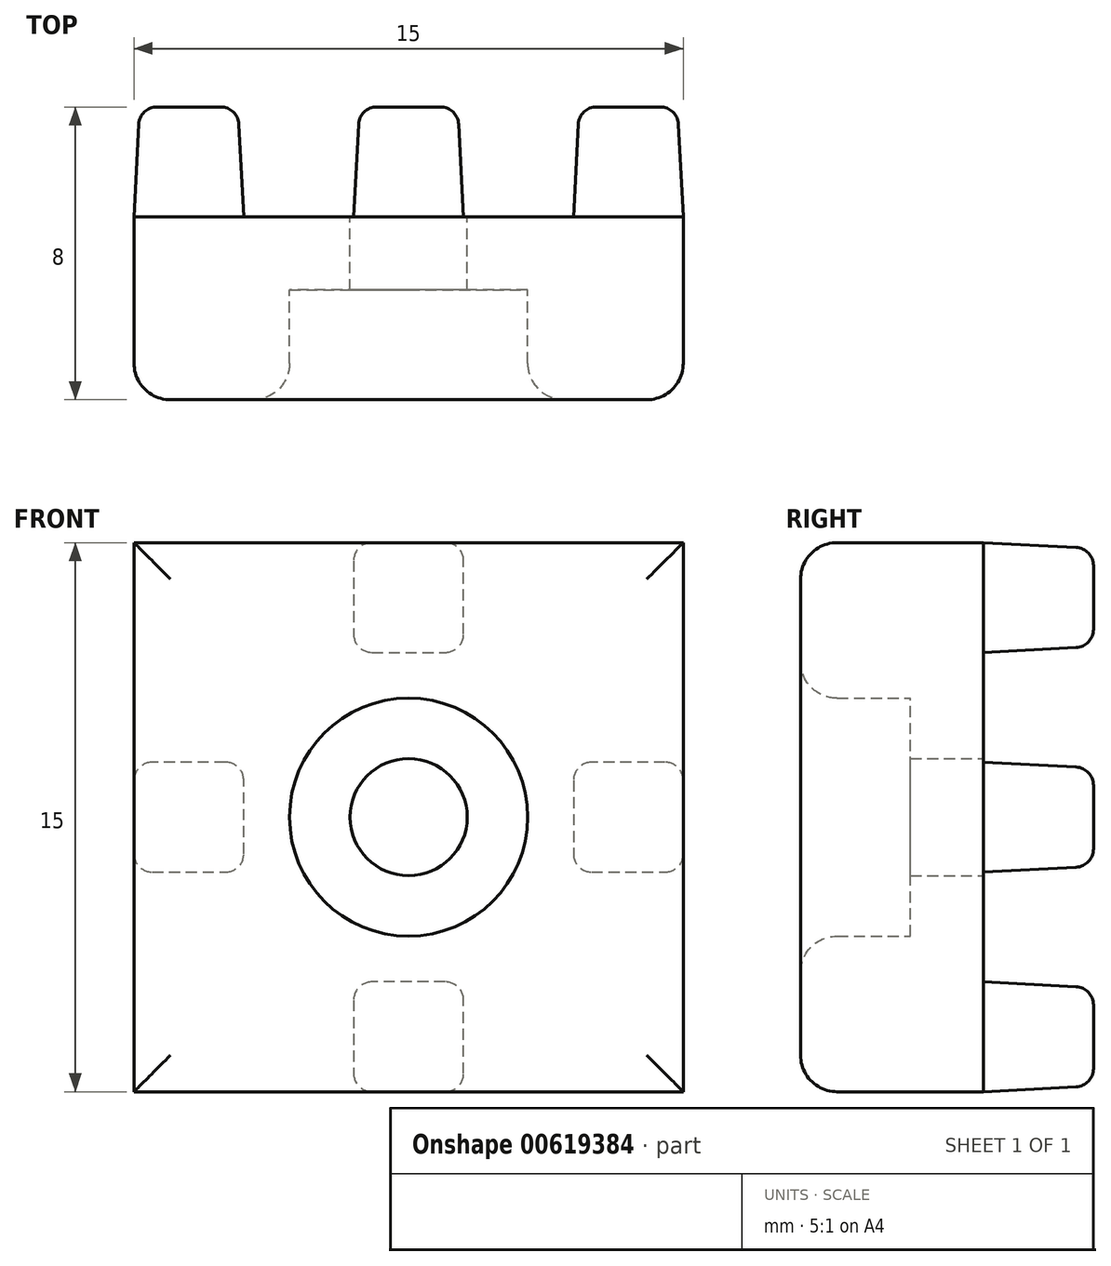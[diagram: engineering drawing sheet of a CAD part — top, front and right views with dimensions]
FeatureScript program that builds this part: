
annotation { "Feature Type Name" : "Feature", "Feature Type Description" : "" }
export const myFeature = defineFeature(function(context is Context, id is Id, definition is map)
    precondition{}
    {
        {
            var Q0;
            Q0=qCreatedBy(makeId("Front.planeOp"),FACE);
            var sketch = newSketch(context, id + "F0", { "sketchPlane" : qUnion([Q0])});
            skLineSegment(sketch, "E0.bottom", {"start": v(0, 0) * mm, "end": v(15, 0) * mm});
            skLineSegment(sketch, "E0.top", {"start": v(0, 15) * mm, "end": v(15, 15) * mm});
            skLineSegment(sketch, "E0.left", {"start": v(0, 0) * mm, "end": v(0, 15) * mm});
            skLineSegment(sketch, "E0.right", {"start": v(15, 0) * mm, "end": v(15, 15) * mm});
            skCircle(sketch, "E1", {"center": v(7.5, 7.5) * mm, "radius": 1.6 * mm});
            skPoint(sketch, "E1.centerSnap0", {"position": v(0, 7.5) * mm});
            skPoint(sketch, "E1.centerSnap1", {"position": v(7.5, 15) * mm});
            skCircle(sketch, "E2", {"center": v(7.5, 7.5) * mm, "radius": 3.25 * mm});
            skLineSegment(sketch, "E3", {"start": v(6, 15) * mm, "end": v(6, 12) * mm});
            skLineSegment(sketch, "E4", {"start": v(6, 12) * mm, "end": v(7.5, 12) * mm});
            skLineSegment(sketch, "E5", {"start": v(7.5, 15) * mm, "end": v(7.5, 12) * mm, "construction": true});
            skLineSegment(sketch, "E6.MirrorCS", {"start": v(9, 12) * mm, "end": v(7.5, 12) * mm});
            skLineSegment(sketch, "E7.MirrorCS", {"start": v(9, 15) * mm, "end": v(9, 12) * mm});
            skLineSegment(sketch, "E8.1.0", {"start": v(3, 6) * mm, "end": v(3, 7.5) * mm});
            skLineSegment(sketch, "E8.1.1", {"start": v(0, 6) * mm, "end": v(3, 6) * mm});
            skLineSegment(sketch, "E8.1.2", {"start": v(3, 9) * mm, "end": v(3, 7.5) * mm});
            skLineSegment(sketch, "E8.1.3", {"start": v(0, 9) * mm, "end": v(3, 9) * mm});
            skLineSegment(sketch, "E8.2.0", {"start": v(9, 3) * mm, "end": v(7.5, 3) * mm});
            skLineSegment(sketch, "E8.2.1", {"start": v(9, 0) * mm, "end": v(9, 3) * mm});
            skLineSegment(sketch, "E8.2.2", {"start": v(6, 3) * mm, "end": v(7.5, 3) * mm});
            skLineSegment(sketch, "E8.2.3", {"start": v(6, 0) * mm, "end": v(6, 3) * mm});
            skLineSegment(sketch, "E8.3.0", {"start": v(12, 9) * mm, "end": v(12, 7.5) * mm});
            skLineSegment(sketch, "E8.3.1", {"start": v(15, 9) * mm, "end": v(12, 9) * mm});
            skLineSegment(sketch, "E8.3.2", {"start": v(12, 6) * mm, "end": v(12, 7.5) * mm});
            skLineSegment(sketch, "E8.3.3", {"start": v(15, 6) * mm, "end": v(12, 6) * mm});
            skSolve(sketch);
        }
        {
            var Q0;
            Q0=makeQuery(id+"F0.imprint","IMPRINT",FACE,{"disambiguationData":[TD([[makeQuery(id+"F0.imprint","IMPRINT",EDGE,{"derivedFrom":sQuery(id+"F0.wireOp",EDGE,"E0.bottom")}),1.0]])]});
            var Q1;
            Q1=makeQuery(id+"F0.imprint","IMPRINT",FACE,{"disambiguationData":[TD([[makeQuery(id+"F0.imprint","IMPRINT",EDGE,{"derivedFrom":sQuery(id+"F0.wireOp",EDGE,"E8.2.0")}),1.0]])]});
            var Q2;
            Q2=makeQuery(id+"F0.imprint","IMPRINT",FACE,{"disambiguationData":[TD([[makeQuery(id+"F0.imprint","IMPRINT",EDGE,{"derivedFrom":sQuery(id+"F0.wireOp",EDGE,"E8.1.0")}),1.0]])]});
            var Q3;
            {var subQ0=sQuery(id+"F0.wireOp",EDGE,"E3");Q3=makeQuery(id+"F0.imprint","IMPRINT",FACE,{"disambiguationData":[TD([[makeQuery(id+"F0.imprint","IMPRINT",EDGE,{"derivedFrom":subQ0}),1.0]])]});}
            var Q4;
            Q4=makeQuery(id+"F0.imprint","IMPRINT",FACE,{"disambiguationData":[TD([[makeQuery(id+"F0.imprint","IMPRINT",EDGE,{"derivedFrom":sQuery(id+"F0.wireOp",EDGE,"E8.3.0")}),1.0]])]});
            extrude(context, id + "F1", {"entities" : qUnion([Q0, Q1, Q2, Q3, Q4]), "depth" : 5 * mm, "offsetDistance" : 25 * mm});
        }
        {
            var Q0;
            Q0=makeQuery(id+"F0.imprint","IMPRINT",FACE,{"disambiguationData":[TD([[makeQuery(id+"F0.imprint","IMPRINT",EDGE,{"derivedFrom":sQuery(id+"F0.wireOp",EDGE,"E1")}),-1.0]])]});
            extrude(context, id + "F2", {"entities" : qUnion([Q0]), "operationType" : NewBodyOperationType.ADD, "depth" : 2 * mm, "offsetDistance" : 25 * mm});
        }
        {
            var Q0;
            Q0=makeQuery(id+"F0.imprint","IMPRINT",FACE,{"disambiguationData":[TD([[makeQuery(id+"F0.imprint","IMPRINT",EDGE,{"derivedFrom":sQuery(id+"F0.wireOp",EDGE,"E8.2.0")}),1.0]])]});
            var Q1;
            Q1=makeQuery(id+"F0.imprint","IMPRINT",FACE,{"disambiguationData":[TD([[makeQuery(id+"F0.imprint","IMPRINT",EDGE,{"derivedFrom":sQuery(id+"F0.wireOp",EDGE,"E8.1.0")}),1.0]])]});
            var Q2;
            {var subQ0=sQuery(id+"F0.wireOp",EDGE,"E3");Q2=makeQuery(id+"F0.imprint","IMPRINT",FACE,{"disambiguationData":[TD([[makeQuery(id+"F0.imprint","IMPRINT",EDGE,{"derivedFrom":subQ0}),1.0]])]});}
            var Q3;
            Q3=makeQuery(id+"F0.imprint","IMPRINT",FACE,{"disambiguationData":[TD([[makeQuery(id+"F0.imprint","IMPRINT",EDGE,{"derivedFrom":sQuery(id+"F0.wireOp",EDGE,"E8.3.0")}),1.0]])]});
            extrude(context, id + "F3", {"entities" : qUnion([Q0, Q1, Q2, Q3]), "operationType" : NewBodyOperationType.ADD, "oppositeDirection" : true, "depth" : 3 * mm, "offsetDistance" : 25 * mm, "hasDraft" : true, "draftAngle" : 3 * degree, "draftPullDirection" : true});
        }
        {
            var Q0;
            Q0=makeQuery(id+"F1.opExtrude","CAP_EDGE",EDGE,{"disambiguationData":[OSD([sQuery(id+"F0.wireOp",EDGE,"E0.top")])],"isStart":false});
            var Q1;
            Q1=makeQuery(id+"F1.opExtrude","CAP_EDGE",EDGE,{"disambiguationData":[OSD([sQuery(id+"F0.wireOp",EDGE,"E0.right")])],"isStart":false});
            var Q2;
            Q2=makeQuery(id+"F1.opExtrude","CAP_EDGE",EDGE,{"disambiguationData":[OSD([sQuery(id+"F0.wireOp",EDGE,"E0.bottom")])],"isStart":false});
            var Q3;
            Q3=makeQuery(id+"F1.opExtrude","CAP_EDGE",EDGE,{"disambiguationData":[OSD([sQuery(id+"F0.wireOp",EDGE,"E0.left")])],"isStart":false});
            var Q4;
            Q4=makeQuery(id+"F1.opExtrude","CAP_EDGE",EDGE,{"disambiguationData":[OSD([sQuery(id+"F0.wireOp",EDGE,"E2")])],"isStart":false});
            fillet(context, id + "F4", {"entities" : qUnion([Q0, Q1, Q2, Q3, Q4]), "radius" : 1 * mm, "tangentPropagation" : true, "allowEdgeOverflow" : false});
        }
        {
            var Q0;
            Q0=makeQuery(id+"F3.opExtrude","CAP_EDGE",EDGE,{"disambiguationData":[OSD([sQuery(id+"F0.wireOp",EDGE,"E8.2.0"),sQuery(id+"F0.wireOp",EDGE,"E8.2.2")])],"isStart":false});
            var Q1;
            Q1=makeQuery(id+"F3.opExtrude","CAP_EDGE",EDGE,{"disambiguationData":[OSD([sQuery(id+"F0.wireOp",EDGE,"E8.2.3")])],"isStart":false});
            var Q2;
            Q2=makeQuery(id+"F3.opExtrude","CAP_EDGE",EDGE,{"disambiguationData":[OSD([sQuery(id+"F0.wireOp",EDGE,"E0.bottom")])],"isStart":false});
            var Q3;
            Q3=makeQuery(id+"F3.opExtrude","CAP_EDGE",EDGE,{"disambiguationData":[OSD([sQuery(id+"F0.wireOp",EDGE,"E8.2.1")])],"isStart":false});
            var Q4;
            Q4=makeQuery(id+"F3.opExtrude","SWEPT_EDGE",EDGE,{"disambiguationData":[OSD([sQuery(id+"F0.wireOp",EDGE,"E8.2.2"),sQuery(id+"F0.wireOp",EDGE,"E8.2.3")])]});
            var Q5;
            Q5=makeQuery(id+"F3.opExtrude","SWEPT_EDGE",EDGE,{"disambiguationData":[OSD([sQuery(id+"F0.wireOp",EDGE,"E8.2.0"),sQuery(id+"F0.wireOp",EDGE,"E8.2.1")])]});
            var Q6;
            Q6=makeQuery(id+"F3.opExtrude","SWEPT_EDGE",EDGE,{"disambiguationData":[OSD([sQuery(id+"F0.wireOp",EDGE,"E0.bottom"),sQuery(id+"F0.wireOp",EDGE,"E8.2.1")])]});
            var Q7;
            Q7=makeQuery(id+"F3.opExtrude","SWEPT_EDGE",EDGE,{"disambiguationData":[OSD([sQuery(id+"F0.wireOp",EDGE,"E0.bottom"),sQuery(id+"F0.wireOp",EDGE,"E8.2.3")])]});
            var Q8;
            Q8=makeQuery(id+"F3.opExtrude","SWEPT_EDGE",EDGE,{"disambiguationData":[OSD([sQuery(id+"F0.wireOp",EDGE,"E0.left"),sQuery(id+"F0.wireOp",EDGE,"E8.1.1")])]});
            var Q9;
            Q9=makeQuery(id+"F3.opExtrude","SWEPT_EDGE",EDGE,{"disambiguationData":[OSD([sQuery(id+"F0.wireOp",EDGE,"E0.left"),sQuery(id+"F0.wireOp",EDGE,"E8.1.3")])]});
            var Q10;
            Q10=makeQuery(id+"F3.opExtrude","SWEPT_EDGE",EDGE,{"disambiguationData":[OSD([sQuery(id+"F0.wireOp",EDGE,"E8.1.2"),sQuery(id+"F0.wireOp",EDGE,"E8.1.3")])]});
            var Q11;
            Q11=makeQuery(id+"F3.opExtrude","SWEPT_EDGE",EDGE,{"disambiguationData":[OSD([sQuery(id+"F0.wireOp",EDGE,"E8.1.0"),sQuery(id+"F0.wireOp",EDGE,"E8.1.1")])]});
            var Q12;
            Q12=makeQuery(id+"F3.opExtrude","CAP_EDGE",EDGE,{"disambiguationData":[OSD([sQuery(id+"F0.wireOp",EDGE,"E8.1.0"),sQuery(id+"F0.wireOp",EDGE,"E8.1.2")])],"isStart":false});
            var Q13;
            Q13=makeQuery(id+"F3.opExtrude","CAP_EDGE",EDGE,{"disambiguationData":[OSD([sQuery(id+"F0.wireOp",EDGE,"E8.1.1")])],"isStart":false});
            var Q14;
            Q14=makeQuery(id+"F3.opExtrude","CAP_EDGE",EDGE,{"disambiguationData":[OSD([sQuery(id+"F0.wireOp",EDGE,"E0.left")])],"isStart":false});
            var Q15;
            Q15=makeQuery(id+"F3.opExtrude","CAP_EDGE",EDGE,{"disambiguationData":[OSD([sQuery(id+"F0.wireOp",EDGE,"E8.1.3")])],"isStart":false});
            var Q16;
            Q16=makeQuery(id+"F3.opExtrude","SWEPT_EDGE",EDGE,{"disambiguationData":[OSD([sQuery(id+"F0.wireOp",EDGE,"E0.top"),sQuery(id+"F0.wireOp",EDGE,"E3")])]});
            var Q17;
            Q17=makeQuery(id+"F3.opExtrude","SWEPT_EDGE",EDGE,{"disambiguationData":[OSD([sQuery(id+"F0.wireOp",EDGE,"E3"),sQuery(id+"F0.wireOp",EDGE,"E4")])]});
            var Q18;
            Q18=makeQuery(id+"F3.opExtrude","CAP_EDGE",EDGE,{"disambiguationData":[OSD([sQuery(id+"F0.wireOp",EDGE,"E4"),sQuery(id+"F0.wireOp",EDGE,"E6.MirrorCS")])],"isStart":false});
            var Q19;
            Q19=makeQuery(id+"F3.opExtrude","CAP_EDGE",EDGE,{"disambiguationData":[OSD([sQuery(id+"F0.wireOp",EDGE,"E3")])],"isStart":false});
            var Q20;
            Q20=makeQuery(id+"F3.opExtrude","CAP_EDGE",EDGE,{"disambiguationData":[OSD([sQuery(id+"F0.wireOp",EDGE,"E0.top")])],"isStart":false});
            var Q21;
            Q21=makeQuery(id+"F3.opExtrude","CAP_EDGE",EDGE,{"disambiguationData":[OSD([sQuery(id+"F0.wireOp",EDGE,"E7.MirrorCS")])],"isStart":false});
            var Q22;
            Q22=makeQuery(id+"F3.opExtrude","SWEPT_EDGE",EDGE,{"disambiguationData":[OSD([sQuery(id+"F0.wireOp",EDGE,"E0.top"),sQuery(id+"F0.wireOp",EDGE,"E7.MirrorCS")])]});
            var Q23;
            Q23=makeQuery(id+"F3.opExtrude","SWEPT_EDGE",EDGE,{"disambiguationData":[OSD([sQuery(id+"F0.wireOp",EDGE,"E6.MirrorCS"),sQuery(id+"F0.wireOp",EDGE,"E7.MirrorCS")])]});
            var Q24;
            Q24=makeQuery(id+"F3.opExtrude","SWEPT_EDGE",EDGE,{"disambiguationData":[OSD([sQuery(id+"F0.wireOp",EDGE,"E8.3.0"),sQuery(id+"F0.wireOp",EDGE,"E8.3.1")])]});
            var Q25;
            Q25=makeQuery(id+"F3.opExtrude","CAP_EDGE",EDGE,{"disambiguationData":[OSD([sQuery(id+"F0.wireOp",EDGE,"E8.3.1")])],"isStart":false});
            var Q26;
            Q26=makeQuery(id+"F3.opExtrude","SWEPT_EDGE",EDGE,{"disambiguationData":[OSD([sQuery(id+"F0.wireOp",EDGE,"E0.right"),sQuery(id+"F0.wireOp",EDGE,"E8.3.1")])]});
            var Q27;
            Q27=makeQuery(id+"F3.opExtrude","SWEPT_EDGE",EDGE,{"disambiguationData":[OSD([sQuery(id+"F0.wireOp",EDGE,"E0.right"),sQuery(id+"F0.wireOp",EDGE,"E8.3.3")])]});
            var Q28;
            Q28=makeQuery(id+"F3.opExtrude","CAP_EDGE",EDGE,{"disambiguationData":[OSD([sQuery(id+"F0.wireOp",EDGE,"E0.right")])],"isStart":false});
            var Q29;
            Q29=makeQuery(id+"F3.opExtrude","CAP_EDGE",EDGE,{"disambiguationData":[OSD([sQuery(id+"F0.wireOp",EDGE,"E8.3.3")])],"isStart":false});
            var Q30;
            Q30=makeQuery(id+"F3.opExtrude","SWEPT_EDGE",EDGE,{"disambiguationData":[OSD([sQuery(id+"F0.wireOp",EDGE,"E8.3.2"),sQuery(id+"F0.wireOp",EDGE,"E8.3.3")])]});
            var Q31;
            Q31=makeQuery(id+"F3.opExtrude","CAP_EDGE",EDGE,{"disambiguationData":[OSD([sQuery(id+"F0.wireOp",EDGE,"E8.3.0"),sQuery(id+"F0.wireOp",EDGE,"E8.3.2")])],"isStart":false});
            fillet(context, id + "F5", {"entities" : qUnion([Q0, Q1, Q2, Q3, Q4, Q5, Q6, Q7, Q8, Q9, Q10, Q11, Q12, Q13, Q14, Q15, Q16, Q17, Q18, Q19, Q20, Q21, Q22, Q23, Q24, Q25, Q26, Q27, Q28, Q29, Q30, Q31]), "radius" : 0.5 * mm, "tangentPropagation" : true, "allowEdgeOverflow" : false});
        }
    });
